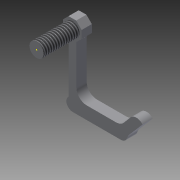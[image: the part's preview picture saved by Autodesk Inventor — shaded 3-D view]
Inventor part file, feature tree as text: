
AUTODESK INVENTOR PART (.ipt)
format: ipt  version: 2015 SP2 (Build 190223200, 223)  size: 147,968 bytes
history: native  units: mm
features: sketch x15, extrude x8, fillet x3, thread x1
ambient origin geometry x8: Origin, YZ Plane, XZ Plane, XY Plane, X Axis, Y Axis, Z Axis, Center Point
bodies: Solid1 (feature_tree)
feature tree (27):
  sketch  "Sketch1"  dims[d0=2.8mm d1=7.0mm d2=0.0mm]
  sketch  "Sketch2"  dims[d4=2.0mm d5=0.0mm d6=10.0mm d7=0.0mm]
  extrude  "Extrusion1"  Depth=7.0mm TaperAngle=0.0deg
  extrude  "Extrusion2"  Depth=10.0mm TaperAngle=0.0deg
  extrude  "Extrusion3"  Depth=2.0mm TaperAngle=0.0deg
  sketch  "Sketch5"  dims[d18=2.0mm d19=0.0mm d20=8.726646mm]
  sketch  "Sketch6"  dims[d21=2.0mm d22=0.0mm d23=2.0mm]
  thread  "Thread1"  [1 undecoded]
  extrude  "Extrusion4"  Depth=2.0mm
  sketch  "Sketch8"
  sketch  "Sketch9"
  extrude  "Extrusion5"  Depth=2.0mm
  sketch  "Sketch11"
  sketch  "Sketch12"
  extrude  "Extrusion6"  Depth=2.0mm
  extrude  "Extrusion7"  Depth=2.0mm
  extrude  "Extrusion8"  [1 undecoded]
  fillet  "Fillet1"  [1 undecoded]
  fillet  "Fillet2"  [1 undecoded]
  fillet  "Fillet3"  [1 undecoded]
  sketch  "Sketch3"  dims[d8=10.0mm d9=0.0mm d10=2.0mm d11=0.0mm d12=4.0mm d13=0.0mm]
  sketch  "Sketch4"  dims[d15=2.0mm d16=0.0mm d17=2.483mm]
  sketch  "Sketch7"  dims[d24=2.0mm d25=2.0mm]
  sketch  "Sketch10"
  sketch  "Sketch13"
  sketch  "Sketch14"
  sketch  "Sketch15"
note: 5 required parameter values undecoded (feature->parameter linkage not recoverable at this tier; creation-order binding heuristic only, values carry confidence <= 0.55)
